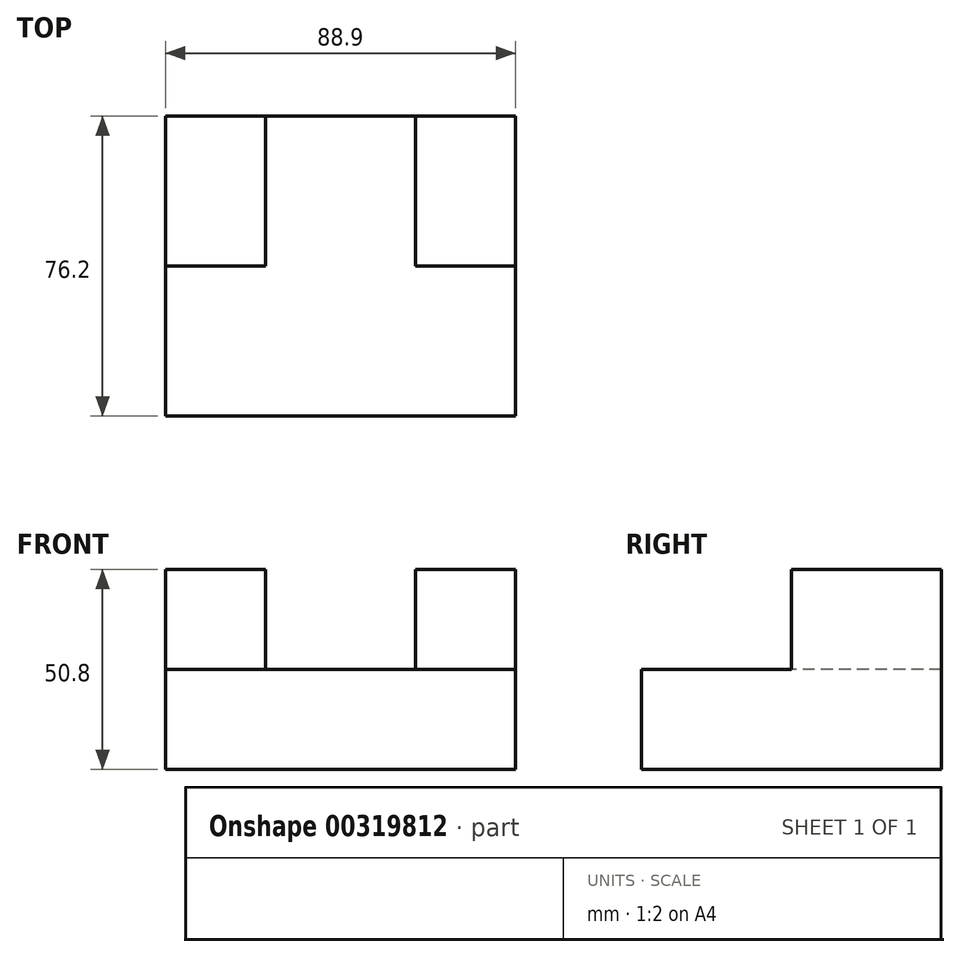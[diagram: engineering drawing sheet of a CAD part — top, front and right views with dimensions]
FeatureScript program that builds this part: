
annotation { "Feature Type Name" : "Feature", "Feature Type Description" : "" }
export const myFeature = defineFeature(function(context is Context, id is Id, definition is map)
    precondition{}
    {
        {
            var Q0;
            Q0=qCreatedBy(makeId("Top.planeOp"),FACE);
            var sketch = newSketch(context, id + "F0", { "sketchPlane" : qUnion([Q0])});
            skLineSegment(sketch, "E0.bottom", {"start": v(-44.38, 27.46) * mm, "end": v(44.52, 27.46) * mm});
            skLineSegment(sketch, "E0.top", {"start": v(-44.38, -48.74) * mm, "end": v(44.52, -48.74) * mm});
            skLineSegment(sketch, "E0.left", {"start": v(-44.38, 27.46) * mm, "end": v(-44.38, -48.74) * mm});
            skLineSegment(sketch, "E0.right", {"start": v(44.52, 27.46) * mm, "end": v(44.52, -48.74) * mm});
            skSolve(sketch);
        }
        {
            var Q0;
            Q0=makeQuery(id+"F0.imprint","IMPRINT",FACE,{"disambiguationData":[TD([[makeQuery(id+"F0.imprint","IMPRINT",EDGE,{"derivedFrom":sQuery(id+"F0.wireOp",EDGE,"E0.bottom")}),-1.0]])]});
            extrude(context, id + "F1", {"entities" : qUnion([Q0]), "depth" : 25.4 * mm});
        }
        {
            var Q0;
            Q0=makeQuery(id+"F1.opExtrude","CAP_FACE",FACE,{"disambiguationData":[OSD([sQuery(id+"F0.wireOp",EDGE,"E0.bottom"),sQuery(id+"F0.wireOp",EDGE,"E0.top"),sQuery(id+"F0.wireOp",EDGE,"E0.left"),sQuery(id+"F0.wireOp",EDGE,"E0.right")])],"isStart":false});
            var sketch = newSketch(context, id + "F2", { "sketchPlane" : qUnion([Q0])});
            skLineSegment(sketch, "E1", {"start": v(-18.98, 27.46) * mm, "end": v(-18.98, -10.64) * mm});
            skLineSegment(sketch, "E2", {"start": v(-18.98, -10.64) * mm, "end": v(-44.38, -10.64) * mm});
            skLineSegment(sketch, "E3", {"start": v(19.12, 27.46) * mm, "end": v(19.12, -10.64) * mm});
            skLineSegment(sketch, "E4", {"start": v(19.12, -10.64) * mm, "end": v(44.52, -10.64) * mm});
            skLineSegment(sketch, "E5", {"start": v(-18.98, 27.46) * mm, "end": v(-44.38, 27.46) * mm});
            skLineSegment(sketch, "E6", {"start": v(-44.38, 27.46) * mm, "end": v(-44.38, -10.64) * mm});
            skLineSegment(sketch, "E7", {"start": v(19.12, 27.46) * mm, "end": v(44.52, 27.46) * mm});
            skLineSegment(sketch, "E8", {"start": v(44.52, 27.46) * mm, "end": v(44.52, -10.64) * mm});
            skSolve(sketch);
        }
        {
            var Q0;
            Q0=makeQuery(id+"F2.imprint","IMPRINT",FACE,{"disambiguationData":[TD([[makeQuery(id+"F2.imprint","IMPRINT",EDGE,{"derivedFrom":sQuery(id+"F2.wireOp",EDGE,"E3")}),1.0]])]});
            var Q1;
            Q1=makeQuery(id+"F2.imprint","IMPRINT",FACE,{"disambiguationData":[TD([[makeQuery(id+"F2.imprint","IMPRINT",EDGE,{"derivedFrom":sQuery(id+"F2.wireOp",EDGE,"E1")}),-1.0]])]});
            extrude(context, id + "F3", {"entities" : qUnion([Q0, Q1]), "operationType" : NewBodyOperationType.ADD, "depth" : 25.4 * mm});
        }
    });
